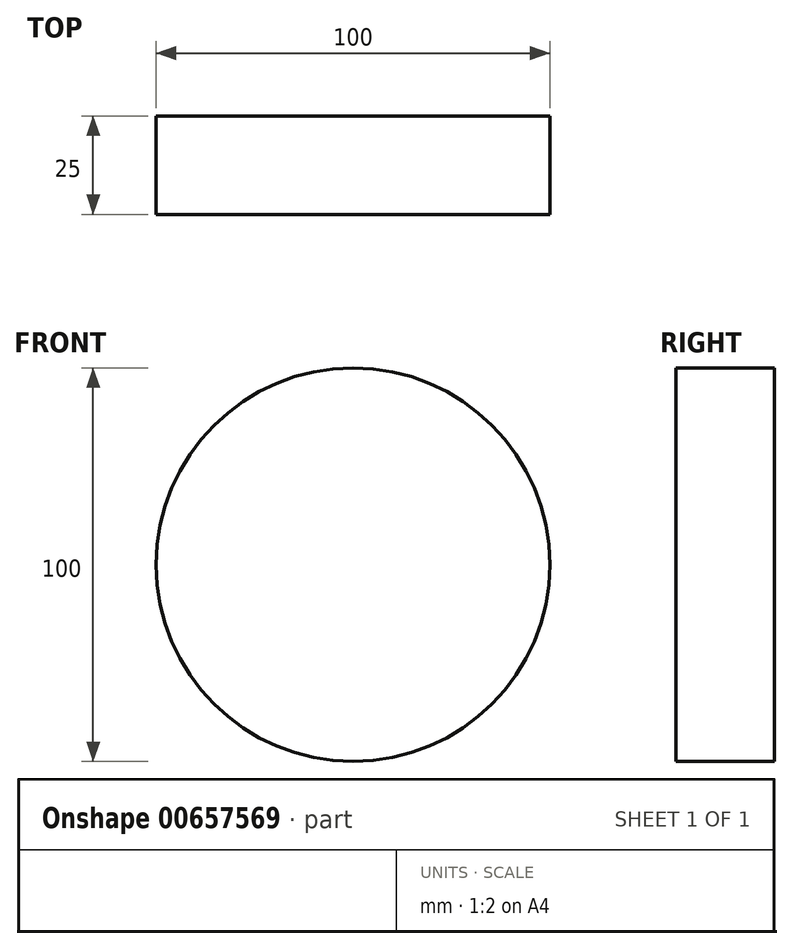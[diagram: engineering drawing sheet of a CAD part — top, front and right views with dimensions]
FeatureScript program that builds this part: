
annotation { "Feature Type Name" : "Feature", "Feature Type Description" : "" }
export const myFeature = defineFeature(function(context is Context, id is Id, definition is map)
    precondition{}
    {
        {
            var Q0;
            Q0=qCreatedBy(makeId("Front.planeOp"),FACE);
            var sketch = newSketch(context, id + "F0", { "sketchPlane" : qUnion([Q0])});
            skCircle(sketch, "E0", {"center": v(0, 0) * mm, "radius": 50 * mm});
            skSolve(sketch);
        }
        {
            var Q0;
            Q0=makeQuery(id+"F0.imprint","IMPRINT",FACE,{"disambiguationData":[TD([[makeQuery(id+"F0.imprint","IMPRINT",EDGE,{"derivedFrom":sQuery(id+"F0.wireOp",EDGE,"E0")}),1.0]])]});
            extrude(context, id + "F1", {"entities" : qUnion([Q0]), "depth" : 25 * mm, "offsetDistance" : 25 * mm});
        }
    });
